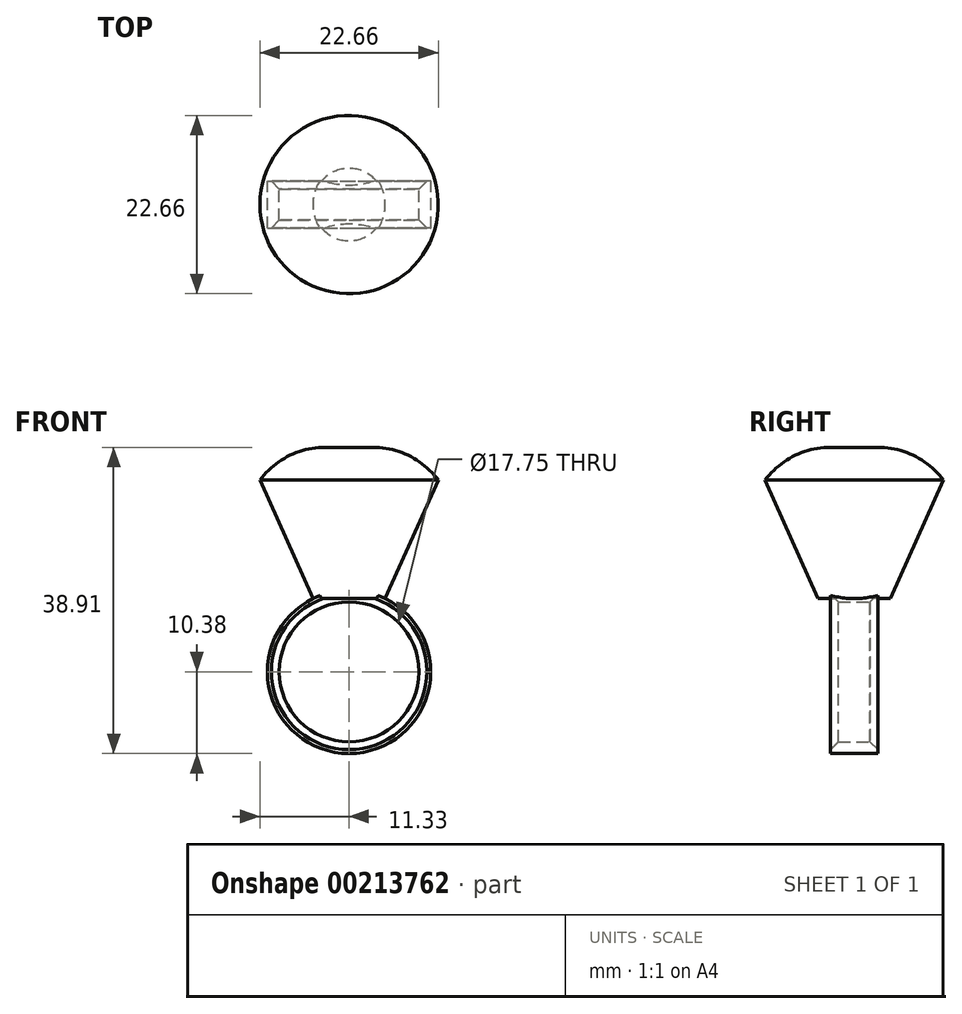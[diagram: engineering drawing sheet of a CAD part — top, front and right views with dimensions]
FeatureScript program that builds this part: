
annotation { "Feature Type Name" : "Feature", "Feature Type Description" : "" }
export const myFeature = defineFeature(function(context is Context, id is Id, definition is map)
    precondition{}
    {
        {
            var Q0;
            Q0=qCreatedBy(makeId("Front.planeOp"),FACE);
            var sketch = newSketch(context, id + "F0", { "sketchPlane" : qUnion([Q0])});
            skCircle(sketch, "E0", {"center": v(0, 0) * mm, "radius": 8.88 * mm});
            skCircle(sketch, "E1.0", {"center": v(0, 0) * mm, "radius": 10.38 * mm});
            skLineSegment(sketch, "E2", {"start": v(0, 9.3) * mm, "end": v(4.6, 9.3) * mm});
            skLineSegment(sketch, "E3", {"start": v(3.01, 28.53) * mm, "end": v(0, 28.53) * mm});
            skPoint(sketch, "E4", {"position": v(0, 9.3) * mm});
            skPoint(sketch, "E5.orphan", {"position": v(-4.6, 9.3) * mm});
            skLineSegment(sketch, "E6", {"start": v(0, 28.53) * mm, "end": v(0, 9.3) * mm});
            skLineSegment(sketch, "E7", {"start": v(4.6, 9.3) * mm, "end": v(11.33, 24.35) * mm});
            skArc(sketch, "E8", {"start": v(11.33, 24.35) * mm, "mid": v(7.67, 27.42) * mm, "end": v(3.01, 28.53) * mm});
            skSolve(sketch);
        }
        {
            var Q0;
            Q0=qCreatedBy(makeId("Top.planeOp"),FACE);
            var sketch = newSketch(context, id + "F1", { "sketchPlane" : qUnion([Q0])});
            skCircle(sketch, "E9", {"center": v(0, 0) * mm, "radius": 4.62 * mm});
            skSolve(sketch);
        }
        {
            var Q0;
            {var subQ2=sQuery(id+"F0.wireOp",EDGE,"E3");Q0=makeQuery(id+"F0.imprint","IMPRINT",FACE,{"disambiguationData":[TD([[makeQuery(id+"F0.imprint","IMPRINT",EDGE,{"derivedFrom":subQ2}),1.0]])]});}
            var Q1;
            {var subQ0=sQuery(id+"F0.wireOp",EDGE,"E2");Q1=makeQuery(id+"F0.imprint","IMPRINT",FACE,{"disambiguationData":[TD([[makeQuery(id+"F0.imprint","IMPRINT",EDGE,{"derivedFrom":subQ0}),1.0]])]});}
            var Q2;
            Q2=sQuery(id+"F1.wireOp",EDGE,"E9");
            revolve(context, id + "F2", {"entities" : qUnion([Q0, Q1]), "axis" : qUnion([Q2]), "revolveType" : RevolveType.FULL});
        }
        {
            var Q0;
            Q0=makeQuery(id+"F0.imprint","IMPRINT",FACE,{"disambiguationData":[TD([[makeQuery(id+"F0.imprint","IMPRINT",EDGE,{"derivedFrom":sQuery(id+"F0.wireOp",EDGE,"E0")}),-1.0]])]});
            var Q1;
            {var subQ0=sQuery(id+"F0.wireOp",EDGE,"E2");Q1=makeQuery(id+"F0.imprint","IMPRINT",FACE,{"disambiguationData":[TD([[makeQuery(id+"F0.imprint","IMPRINT",EDGE,{"derivedFrom":subQ0}),1.0]])]});}
            extrude(context, id + "F3", {"entities" : qUnion([Q0, Q1]), "operationType" : NewBodyOperationType.ADD, "depth" : 3 * mm, "hasSecondDirection" : true, "secondDirectionOppositeDirection" : true, "secondDirectionDepth" : 3 * mm});
        }
        {
            var Q0;
            Q0=makeQuery(id+"F3.opExtrude","CAP_EDGE",EDGE,{"disambiguationData":[OSD([sQuery(id+"F0.wireOp",EDGE,"E0")])],"isStart":false});
            var Q1;
            Q1=makeQuery(id+"F3.opExtrude","CAP_EDGE",EDGE,{"disambiguationData":[OSD([sQuery(id+"F0.wireOp",EDGE,"E0")])],"isStart":true});
            chamfer(context, id + "F4", {"entities" : qUnion([Q0, Q1]), "width" : 1 * mm, "tangentPropagation" : true});
        }
    });
